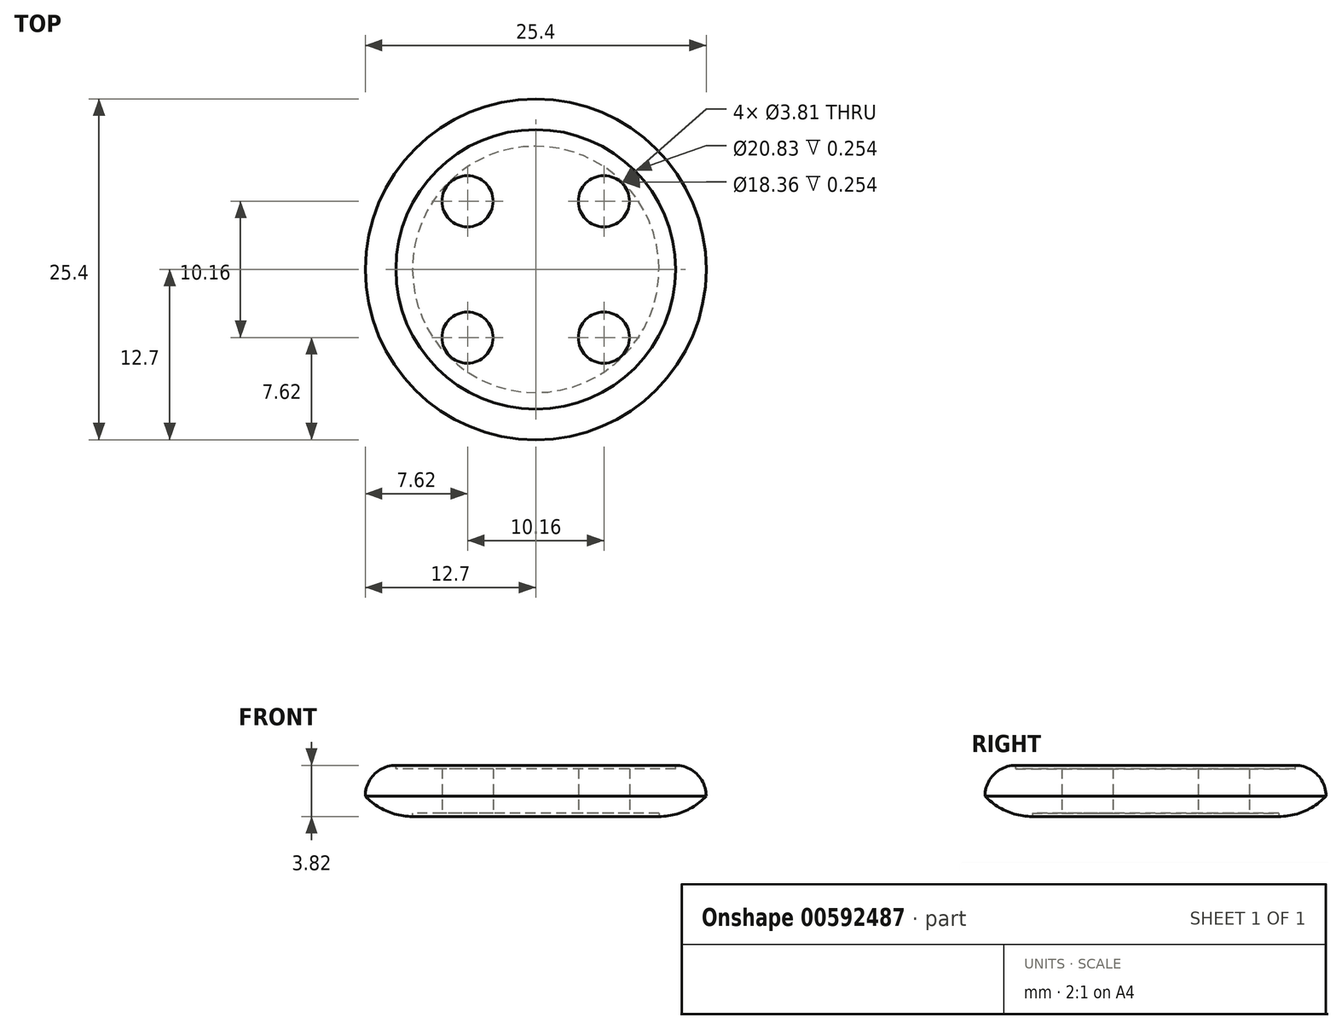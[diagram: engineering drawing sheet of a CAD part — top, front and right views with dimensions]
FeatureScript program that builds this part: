
annotation { "Feature Type Name" : "Feature", "Feature Type Description" : "" }
export const myFeature = defineFeature(function(context is Context, id is Id, definition is map)
    precondition{}
    {
        {
            var Q0;
            Q0=qCreatedBy(makeId("Top.planeOp"),FACE);
            var sketch = newSketch(context, id + "F0", { "sketchPlane" : qUnion([Q0])});
            skCircle(sketch, "E0", {"center": v(0, 0) * mm, "radius": 12.7 * mm});
            skCircle(sketch, "E1", {"center": v(-5.08, 5.08) * mm, "radius": 1.9 * mm});
            skCircle(sketch, "E2", {"center": v(5.08, 5.08) * mm, "radius": 1.9 * mm});
            skCircle(sketch, "E3", {"center": v(5.08, -5.08) * mm, "radius": 1.9 * mm});
            skCircle(sketch, "E4", {"center": v(-5.08, -5.08) * mm, "radius": 1.9 * mm});
            skSolve(sketch);
        }
        {
            var Q0;
            Q0=makeQuery(id+"F0.imprint","IMPRINT",FACE,{"disambiguationData":[TD([[makeQuery(id+"F0.imprint","IMPRINT",EDGE,{"derivedFrom":sQuery(id+"F0.wireOp",EDGE,"E0")}),1.0]])]});
            extrude(context, id + "F1", {"entities" : qUnion([Q0]), "endBound" : BoundingType.SYMMETRIC, "depth" : 3.8 * mm, "offsetDistance" : 25.4 * mm});
        }
        {
            var Q0;
            Q0=makeQuery(id+"F1.opExtrude","CAP_EDGE",EDGE,{"disambiguationData":[OSD([sQuery(id+"F0.wireOp",EDGE,"E0")])],"isStart":false});
            fillet(context, id + "F2", {"entities" : qUnion([Q0]), "radius" : 2.3 * mm, "tangentPropagation" : true, "allowEdgeOverflow" : false});
        }
        {
            var Q0;
            Q0=makeQuery(id+"F1.opExtrude","CAP_EDGE",EDGE,{"disambiguationData":[OSD([sQuery(id+"F0.wireOp",EDGE,"E0")])],"isStart":true});
            fillet(context, id + "F3", {"entities" : qUnion([Q0]), "radius" : 4.83 * mm, "tangentPropagation" : true, "allowEdgeOverflow" : false});
        }
        {
            var Q0;
            Q0=makeQuery(id+"F1.opExtrude","CAP_FACE",FACE,{"disambiguationData":[OSD([sQuery(id+"F0.wireOp",EDGE,"E0"),sQuery(id+"F0.wireOp",EDGE,"E1"),sQuery(id+"F0.wireOp",EDGE,"E2"),sQuery(id+"F0.wireOp",EDGE,"E3"),sQuery(id+"F0.wireOp",EDGE,"E4")])],"isStart":false});
            extrude(context, id + "F4", {"entities" : qUnion([Q0]), "operationType" : NewBodyOperationType.REMOVE, "oppositeDirection" : true, "depth" : 0.25 * mm, "offsetDistance" : 25.4 * mm});
        }
        {
            var Q0;
            Q0=makeQuery(id+"F1.opExtrude","CAP_FACE",FACE,{"disambiguationData":[OSD([sQuery(id+"F0.wireOp",EDGE,"E0"),sQuery(id+"F0.wireOp",EDGE,"E1"),sQuery(id+"F0.wireOp",EDGE,"E2"),sQuery(id+"F0.wireOp",EDGE,"E3"),sQuery(id+"F0.wireOp",EDGE,"E4")])],"isStart":true});
            extrude(context, id + "F5", {"entities" : qUnion([Q0]), "operationType" : NewBodyOperationType.REMOVE, "oppositeDirection" : true, "depth" : 0.25 * mm, "offsetDistance" : 25.4 * mm});
        }
    });
